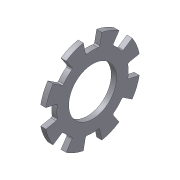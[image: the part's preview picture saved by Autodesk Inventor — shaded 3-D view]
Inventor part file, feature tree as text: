
AUTODESK INVENTOR PART (.ipt)
format: ipt  version: 2016 SP1 (Build 200210100, 210)  size: 133,632 bytes
history: native  units: mm (DEFAULTED — no unit token found)
features: sketch x2, extrude x1, pattern_circular x1
ambient origin geometry x8: Origin, YZ Plane, XZ Plane, XY Plane, X Axis, Y Axis, Z Axis, Center Point
bodies: Solid1 (feature_tree), Body (feature_tree)
feature tree (4):
  extrude  "Cut"  Depth=6.5024mm
  pattern_circular  "Cuts"  [2 undecoded]
  sketch  "Sketch1"  dims[d0=12.954mm d1=6.5024mm]
  sketch  "Sketch2"  dims[d2=0.7112mm d3=0.0mm d4=22.5deg d5=9.7282mm d6=0.7112mm d7=0.0mm d8=0.19431mm d9=80.0mm d11=360.0deg d12=0.0mm d13=0.0mm]
note: 2 required parameter values undecoded (feature->parameter linkage not recoverable at this tier; creation-order binding heuristic only, values carry confidence <= 0.55)
